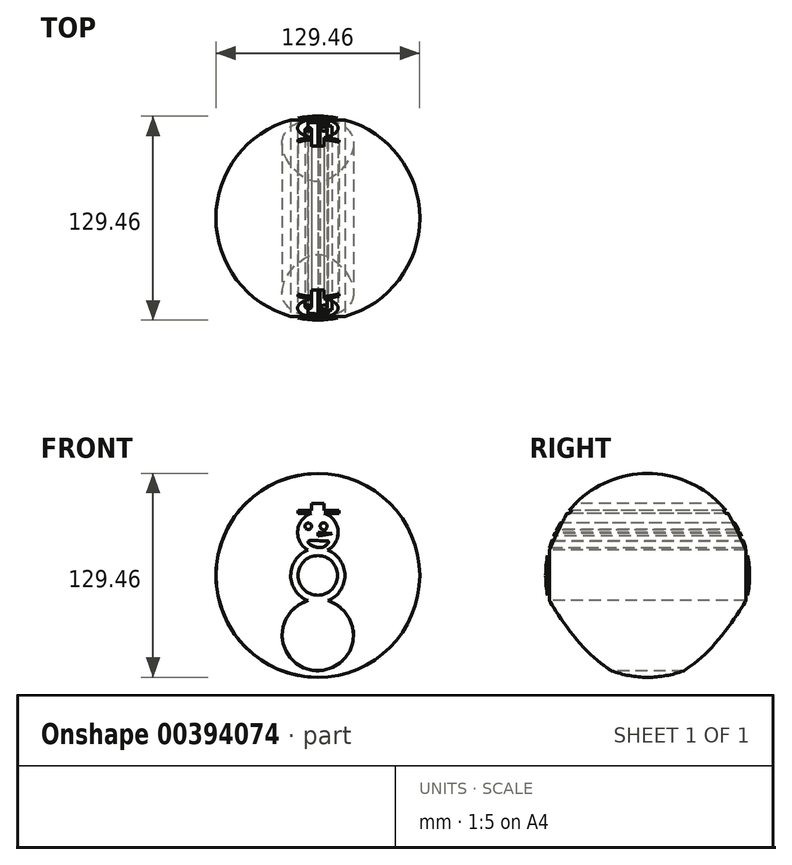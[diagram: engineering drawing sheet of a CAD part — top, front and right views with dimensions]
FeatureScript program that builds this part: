
annotation { "Feature Type Name" : "Feature", "Feature Type Description" : "" }
export const myFeature = defineFeature(function(context is Context, id is Id, definition is map)
    precondition{}
    {
        {
            var Q0;
            Q0=qCreatedBy(makeId("Front.planeOp"),FACE);
            var sketch = newSketch(context, id + "F0", { "sketchPlane" : qUnion([Q0])});
            skCircle(sketch, "E0", {"center": v(0, 0) * mm, "radius": 64.73 * mm});
            skLineSegment(sketch, "E1", {"start": v(0, 64.73) * mm, "end": v(0, -64.73) * mm});
            skSolve(sketch);
        }
        {
            var Q0;
            {var subQ0=sQuery(id+"F0.wireOp",EDGE,"E1");Q0=makeQuery(id+"F0.imprint","IMPRINT",FACE,{"disambiguationData":[TD([[makeQuery(id+"F0.imprint","IMPRINT",EDGE,{"derivedFrom":subQ0}),-1.0]])]});}
            var Q1;
            Q1=sQuery(id+"F0.wireOp",EDGE,"E1");
            revolve(context, id + "F1", {"entities" : qUnion([Q0]), "axis" : qUnion([Q1]), "revolveType" : RevolveType.FULL});
        }
        {
            var Q0;
            Q0=qCreatedBy(makeId("Front.planeOp"),FACE);
            var sketch = newSketch(context, id + "F2", { "sketchPlane" : qUnion([Q0])});
            skArc(sketch, "E2", {"start": v(-3.98, 39.5) * mm, "mid": v(0, 14.44) * mm, "end": v(3.98, 39.5) * mm});
            skArc(sketch, "E3", {"start": v(-6.24, 16.06) * mm, "mid": v(0, -17.23) * mm, "end": v(6.24, 16.06) * mm});
            skArc(sketch, "E4", {"start": v(-6.32, -16.03) * mm, "mid": v(0, -60.53) * mm, "end": v(6.32, -16.03) * mm});
            skLineSegment(sketch, "E5", {"start": v(45.32, 9.9) * mm, "end": v(45.96, 6.89) * mm});
            skCircle(sketch, "E6", {"center": v(3.7, 31.17) * mm, "radius": 2.23 * mm});
            skCircle(sketch, "E7", {"center": v(-6.1, 31.17) * mm, "radius": 2.04 * mm});
            skLineSegment(sketch, "E8", {"start": v(-4.06, 31.17) * mm, "end": v(1.47, 31.17) * mm});
            skLineSegment(sketch, "E9", {"start": v(-8.15, 31.17) * mm, "end": v(-11.52, 32.97) * mm});
            skLineSegment(sketch, "E10", {"start": v(5.86, 30.61) * mm, "end": v(11.05, 33.83) * mm});
            skLineSegment(sketch, "E11", {"start": v(-12.4, 39.5) * mm, "end": v(13.32, 39.5) * mm});
            skLineSegment(sketch, "E12.bottom", {"start": v(-3.98, 39.5) * mm, "end": v(4.07, 39.5) * mm});
            skLineSegment(sketch, "E12.top", {"start": v(-3.98, 45.79) * mm, "end": v(4.07, 45.79) * mm});
            skLineSegment(sketch, "E12.left", {"start": v(-3.98, 39.5) * mm, "end": v(-3.98, 45.79) * mm});
            skLineSegment(sketch, "E12.right", {"start": v(4.07, 39.5) * mm, "end": v(4.07, 45.79) * mm});
            skFitSpline(sketch, "E13", {"points": [v(-6.24, 21.55) * mm, v(5.55, 21.74) * mm, v(6.84, 21.55) * mm, v(2.03, 17.67) * mm, v(-6.24, 21.55) * mm]});
            skLineSegment(sketch, "E14", {"start": v(0, 25.07) * mm, "end": v(9.06, 26.55) * mm});
            skLineSegment(sketch, "E15", {"start": v(9.06, 26.55) * mm, "end": v(0, 27.29) * mm});
            skLineSegment(sketch, "E16", {"start": v(0, 25.07) * mm, "end": v(0, 27.29) * mm});
            skLineSegment(sketch, "E17", {"start": v(-38.85, -47.82) * mm, "end": v(-20.38, -47.82) * mm});
            skLineSegment(sketch, "E18.trimOffspring", {"start": v(20.38, -47.82) * mm, "end": v(43.1, -47.82) * mm});
            skLineSegment(sketch, "E19.bottom", {"start": v(13.32, 39.5) * mm, "end": v(4.07, 39.5) * mm});
            skLineSegment(sketch, "E19.top", {"start": v(13.32, 41.15) * mm, "end": v(4.07, 41.15) * mm});
            skLineSegment(sketch, "E19.left", {"start": v(13.32, 39.5) * mm, "end": v(13.32, 41.15) * mm});
            skLineSegment(sketch, "E19.right", {"start": v(4.07, 39.5) * mm, "end": v(4.07, 41.15) * mm});
            skLineSegment(sketch, "E20.bottom", {"start": v(-3.98, 39.5) * mm, "end": v(-12.47, 39.5) * mm});
            skLineSegment(sketch, "E20.top", {"start": v(-3.98, 41.15) * mm, "end": v(-12.47, 41.15) * mm});
            skLineSegment(sketch, "E20.left", {"start": v(-3.98, 39.5) * mm, "end": v(-3.98, 41.15) * mm});
            skLineSegment(sketch, "E20.right", {"start": v(-12.47, 39.5) * mm, "end": v(-12.47, 41.15) * mm});
            skSolve(sketch);
        }
        {
            var Q0;
            Q0 = qSketchRegion(id + "F2", true);
            extrude(context, id + "F3", {"entities" : qUnion([Q0]), "operationType" : NewBodyOperationType.REMOVE, "endBound" : BoundingType.SYMMETRIC, "oppositeDirection" : true, "depth" : 127 * mm});
        }
    });
